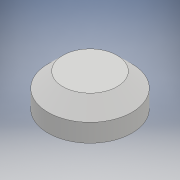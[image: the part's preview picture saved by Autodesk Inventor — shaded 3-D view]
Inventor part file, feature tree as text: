
AUTODESK INVENTOR PART (.ipt)
format: ipt  version: 2018 (Build 220112000, 112)  size: 200,192 bytes
history: native  units: mm
features: extrude x5, sketch x5, fillet x1, chamfer x1, pattern_circular x1
ambient origin geometry x8: Origin, YZ Plane, XZ Plane, XY Plane, X Axis, Y Axis, Z Axis, Center Point
bodies: Solid1 (feature_tree)
feature tree (13):
  extrude  "Extrusion1"  Depth=10.0mm TaperAngle=0.0deg
  extrude  "Extrusion2"  Depth=3.0mm TaperAngle=0.0deg
  extrude  "Extrusion3"  Depth=6.0mm TaperAngle=0.0deg
  extrude  "Extrusion4"  Depth=2.0mm TaperAngle=0.0deg
  fillet  "Fillet2"  Radius=0.7mm
  extrude  "Extrusion5"  Depth=0.6mm
  chamfer  "Chamfer1"  Distance=5.0mm
  pattern_circular  "Circular Pattern2"  [2 undecoded]
  sketch  "Sketch1"  dims[d0=25.5mm d1=10.0mm d2=0.0mm]
  sketch  "Sketch2"  dims[d3=24.0mm d4=3.0mm d5=0.0mm]
  sketch  "Sketch4"  dims[d6=13.5mm d7=6.0mm d8=0.0mm]
  sketch  "Sketch5"  dims[d10=0.7mm d11=2.0mm d12=0.0mm d13=0.7mm]
  sketch  "Sketch6"  dims[d14=1.0mm d15=0.6mm d16=5.0mm d17=5.0mm d18=0.0mm d22=4.5mm d23=2.0mm d24=45.0deg d25=60.0mm d26=360.0deg]
note: 2 required parameter values undecoded (feature->parameter linkage not recoverable at this tier; creation-order binding heuristic only, values carry confidence <= 0.55)
